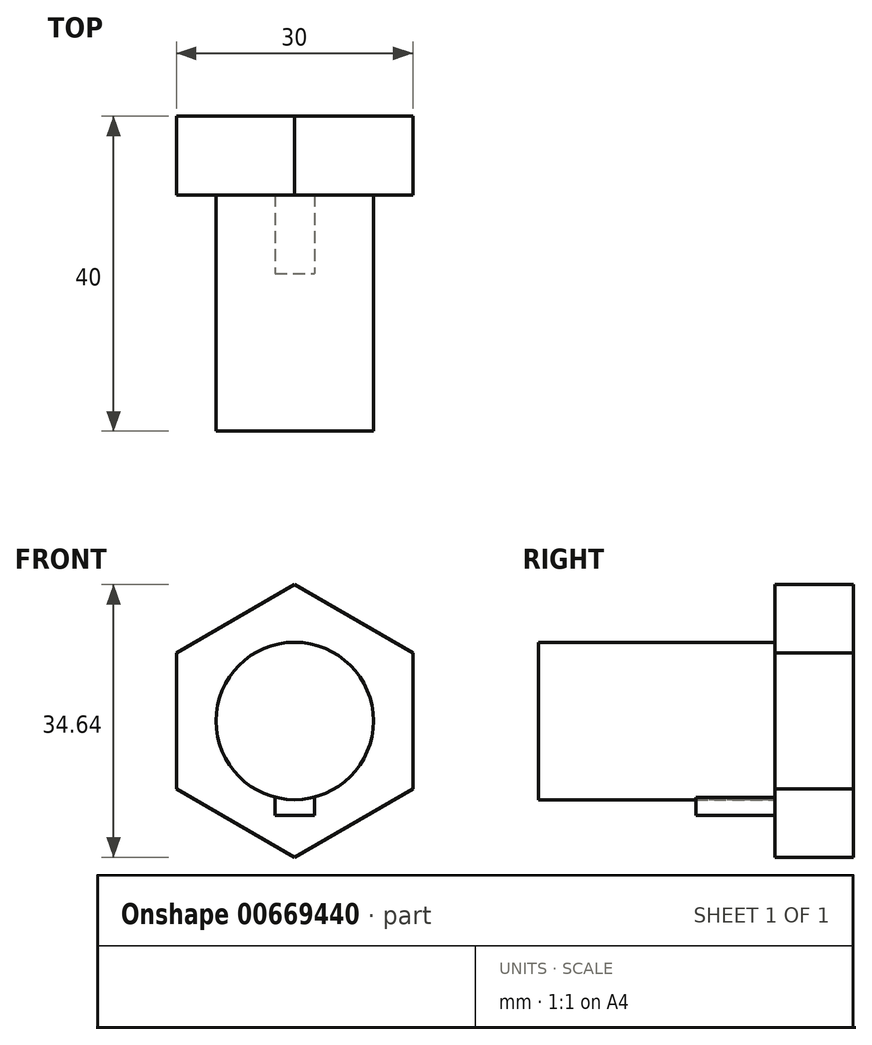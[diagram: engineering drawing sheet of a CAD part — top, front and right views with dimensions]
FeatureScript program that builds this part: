
annotation { "Feature Type Name" : "Feature", "Feature Type Description" : "" }
export const myFeature = defineFeature(function(context is Context, id is Id, definition is map)
    precondition{}
    {
        {
            var Q0;
            Q0=qCreatedBy(makeId("Front.planeOp"),FACE);
            var sketch = newSketch(context, id + "F0", { "sketchPlane" : qUnion([Q0])});
            skLineSegment(sketch, "E0.0", {"start": v(15, 8.66) * mm, "end": v(15, -8.66) * mm});
            skLineSegment(sketch, "E0.4", {"start": v(-15, 8.66) * mm, "end": v(0, 17.32) * mm});
            skLineSegment(sketch, "E0.5", {"start": v(0, 17.32) * mm, "end": v(15, 8.66) * mm});
            skCircle(sketch, "E1", {"center": v(0, 0) * mm, "radius": 10 * mm});
            skLineSegment(sketch, "E2.top", {"start": v(-2.5, -12) * mm, "end": v(2.5, -12) * mm});
            skLineSegment(sketch, "E2.left", {"start": v(-2.5, -9.68) * mm, "end": v(-2.5, -12) * mm});
            skLineSegment(sketch, "E2.right", {"start": v(2.5, -9.68) * mm, "end": v(2.5, -12) * mm});
            skLineSegment(sketch, "E3.5", {"start": v(-15, -8.66) * mm, "end": v(-15, 8.66) * mm});
            skLineSegment(sketch, "E4.4", {"start": v(15, -8.66) * mm, "end": v(0, -17.32) * mm});
            skLineSegment(sketch, "E5.5", {"start": v(0, -17.32) * mm, "end": v(-15, -8.66) * mm});
            skPoint(sketch, "E6.0.midPoint", {"position": v(-15, 0) * mm});
            skSolve(sketch);
        }
        {
            var Q0;
            {var subQ0=sQuery(id+"F0.wireOp",EDGE,"E1");var subQ1=makeQuery(id+"F0.imprint","INTERSECT",VERTEX,{"derivedFrom":[subQ0,sQuery(id+"F0.wireOp",EDGE,"E2.left")]});Q0=makeQuery(id+"F0.imprint","IMPRINT",FACE,{"disambiguationData":[TD([[makeQuery(id+"F0.imprint","IMPRINT",EDGE,{"disambiguationData":[TD([[subQ1,-1.0]])],"derivedFrom":subQ0}),1.0]])]});}
            var Q1;
            Q1=sQuery(id+"F0.wireOp",EDGE,"E1");
            extrude(context, id + "F1", {"entities" : qUnion([Q0]), "surfaceEntities" : qUnion([Q1]), "depth" : 30 * mm, "offsetDistance" : 25 * mm});
        }
        {
            var Q0;
            Q0=makeQuery(id+"F0.imprint","IMPRINT",FACE,{"disambiguationData":[TD([[makeQuery(id+"F0.imprint","IMPRINT",EDGE,{"derivedFrom":sQuery(id+"F0.wireOp",EDGE,"E2.top")}),1.0]])]});
            extrude(context, id + "F2", {"entities" : qUnion([Q0]), "depth" : 10 * mm, "offsetDistance" : 25 * mm});
        }
        {
            var Q0;
            Q0 = qSketchRegion(id + "F0", true);
            var Q1;
            Q1=makeQuery(id+"F2.opExtrude","CAP_FACE",FACE,{"disambiguationData":[OSD([sQuery(id+"F0.wireOp",EDGE,"E1"),sQuery(id+"F0.wireOp",EDGE,"E2.top"),sQuery(id+"F0.wireOp",EDGE,"E2.left"),sQuery(id+"F0.wireOp",EDGE,"E2.right")])],"isStart":false});
            var Q2;
            {var subQ0=sQuery(id+"F0.wireOp",EDGE,"E1");var subQ1=makeQuery(id+"F0.imprint","INTERSECT",VERTEX,{"derivedFrom":[subQ0,sQuery(id+"F0.wireOp",EDGE,"E2.left")]});Q2=makeQuery(id+"F0.imprint","IMPRINT",FACE,{"disambiguationData":[TD([[makeQuery(id+"F0.imprint","IMPRINT",EDGE,{"disambiguationData":[TD([[subQ1,-1.0]])],"derivedFrom":subQ0}),1.0]])]});}
            var Q3;
            Q3=makeQuery(id+"F0.imprint","IMPRINT",FACE,{"disambiguationData":[TD([[makeQuery(id+"F0.imprint","IMPRINT",EDGE,{"derivedFrom":sQuery(id+"F0.wireOp",EDGE,"E2.top")}),1.0]])]});
            extrude(context, id + "F3", {"entities" : qUnion([Q0, Q1, Q2, Q3]), "oppositeDirection" : true, "depth" : 10 * mm, "offsetDistance" : 25 * mm});
        }
    });
